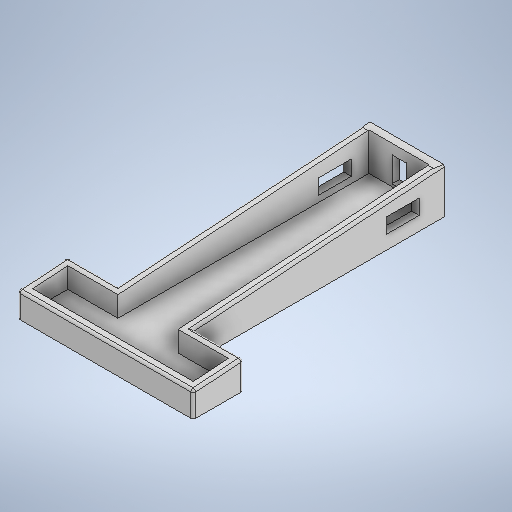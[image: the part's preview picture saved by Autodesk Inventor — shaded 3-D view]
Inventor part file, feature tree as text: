
AUTODESK INVENTOR PART (.ipt)
format: ipt  version: 2025.2 (Build 292293000, 293)  size: 702,976 bytes
history: native  units: mm
features: extrude x8, sketch x8, projected_geometry x7, shell x3, fillet x3, other x1
ambient origin geometry x8: Origin, YZ Plane, XZ Plane, XY Plane, X Axis, Y Axis, Z Axis, Center Point
bodies: Body1 (feature_tree)
feature tree (30):
  other  "Těleso1"
  extrude  "Vysunutí1"  Depth=18.0mm
  shell  "Skořepina1"  Thickness=30.0mm
  extrude  "Vysunutí2"  Depth=120.0mm TaperAngle=0.0deg
  extrude  "Vysunutí3"  Depth=3.0mm
  extrude  "Vysunutí4"  Depth=3.4mm
  shell  "Skořepina2"  Thickness=10.0mm
  extrude  "Vysunutí5"  TaperAngle=0.0deg  [1 undecoded]
  extrude  "Vysunutí6"  Depth=5.6mm
  shell  "Skořepina3"  Thickness=10.0mm
  extrude  "Vysunutí7"  Depth=4.0mm
  extrude  "Vysunutí8"  Depth=9.2mm
  fillet  "Zaoblení1"  [1 undecoded]
  fillet  "Zaoblení2"  Radius=20.0mm
  fillet  "Zaoblení3"  Radius=20.0mm
  sketch  "Náčrt1"
  sketch  "Náčrt2"
  projected_geometry  "Promítnutá smyčka1"
  sketch  "Náčrt3"
  projected_geometry  "Promítnutá smyčka2"
  sketch  "Náčrt4"
  projected_geometry  "Promítnutá smyčka3"
  sketch  "Náčrt5"
  projected_geometry  "Promítnutá smyčka4"
  sketch  "Náčrt6"
  projected_geometry  "Promítnutá smyčka5"
  sketch  "Náčrt7"
  projected_geometry  "Promítnutá smyčka6"
  sketch  "Náčrt8"
  projected_geometry  "Promítnutá smyčka7"
note: 2 required parameter values undecoded (feature->parameter linkage not recoverable at this tier; creation-order binding heuristic only, values carry confidence <= 0.55)
